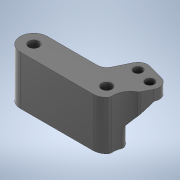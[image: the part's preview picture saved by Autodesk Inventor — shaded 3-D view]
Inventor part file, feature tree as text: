
AUTODESK INVENTOR PART (.ipt)
format: ipt  version: 2020 (Build 240168000, 168)  size: 765,952 bytes
history: native  units: mm
features: extrude x4, sketch x4, chamfer x2, plane x1, mirror x1, fillet x1
ambient origin geometry x8: Origin, YZ Plane, XZ Plane, XY Plane, X Axis, Y Axis, Z Axis, Center Point
bodies: Volumenkörper1 (feature_tree)
feature tree (13):
  extrude  "Extrusion1"  Depth=5.0mm
  extrude  "Extrusion2"  Depth=23.5mm TaperAngle=0.0deg
  chamfer  "Fase1"  Distance=2.5mm
  extrude  "Extrusion3"  Depth=2.0mm
  plane  "Arbeitsebene1"
  mirror  "Spiegeln1"
  chamfer  "Fase2"  Distance=5.0mm
  extrude  "Extrusion4"  Depth=2.0mm TaperAngle=45.0deg
  fillet  "Rundung2"  Radius=7.0mm
  sketch  "Skizze1"  dims[d0=35.0mm d1=5.0mm]
  sketch  "Skizze2"  dims[d2=13.0mm d3=23.5mm d4=0.0mm]
  sketch  "Skizze3"  dims[d5=8.0mm]
  sketch  "Skizze4"  dims[d6=4.2mm d11=2.5mm d12=11.0mm d13=5.0mm d14=0.0mm d15=9.75mm d16=2.0mm d17=45.0deg d19=7.0mm d20=5.0mm d21=0.0mm d22=2.626001mm d23=14.0mm d25=8.5mm d26=5.0mm d27=0.5mm d28=2.0mm d29=45.0deg d30=17.0mm d31=6.8mm d32=14.0mm d33=0.0mm d34=0.0mm d35=2.0mm]
